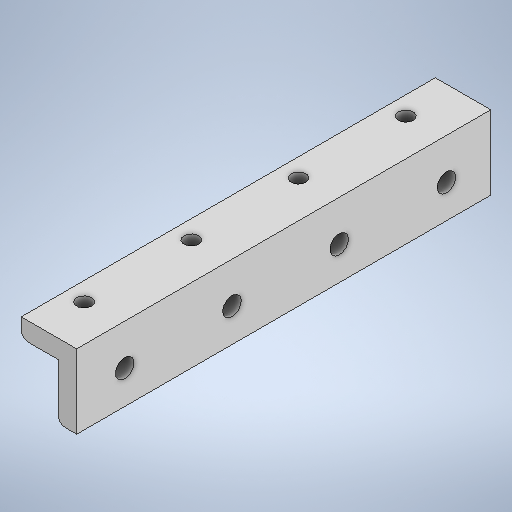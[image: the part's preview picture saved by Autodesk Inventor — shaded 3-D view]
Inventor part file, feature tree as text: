
AUTODESK INVENTOR PART (.ipt)
format: ipt  version: 2025.1 (Build 291241000, 241)  size: 268,800 bytes
history: native  units: mm
features: sketch x3, hole x2, extrude x1, fillet x1
ambient origin geometry x8: Origin, YZ Plane, XZ Plane, XY Plane, X Axis, Y Axis, Z Axis, Center Point
bodies: Volumenkörper1 (feature_tree)
feature tree (7):
  extrude  "Extrusion1"  Depth=15.0mm
  hole  "Bohrung1"  [1 undecoded]
  hole  "Bohrung2"  [1 undecoded]
  fillet  "Rundung1"  Radius=29.0mm
  sketch  "Skizze2"  dims[d6=5.0mm d7=15.0mm]
  sketch  "Skizze3"  dims[d8=5.0mm d9=10.0mm]
  sketch  "Skizze4"  dims[d10=112.0mm d11=0.0mm d12=13.0mm d13=29.0mm d14=29.0mm d15=29.0mm d16=4.0mm d17=12.0mm d18=5.0mm d19=2.0mm d20=90.0deg d21=8.0mm d22=0.0mm d23=5.0mm d24=6.0mm d25=4.0mm d26=2.0mm d27=90.0deg d28=8.0mm d29=0.0mm d30=12.0mm d31=29.0mm d32=29.0mm d33=29.0mm d38=2.0mm d39=10.0mm d40=11.0mm]
note: 2 required parameter values undecoded (feature->parameter linkage not recoverable at this tier; creation-order binding heuristic only, values carry confidence <= 0.55)
